# Revit family: Centro
name_source: partatom
category: Mechanical Equipment
units: mm (PartAtom-declared; Revit-internal decimal feet)

## family parameters
Always vertical = Yes
Classification = None
Cut with Voids When Loaded = No
Part Type = Normal
Room Calculation Point = No
Round Connector Dimension = Use Diameter
Shared = No
Work Plane-Based = No

## types (65) — shared parameters
00_20_Manufacturer = Blauberg
Description = For round channels
Frequency = 50 Hz
Load Classification = HVAC
Maintenance zone material = <By Category>
Manufacturer = Blauberg
Number of Fase = 1
URL = https://blaubergventilatoren.de
Voltage = 230 V
zero-valued in all types: Default Elevation

## per-type parameters (varying)
- Centro 315: Amperage=1 A; Apparent Load=202 VA; B=414 mm; B1=454 mm; B2=374 mm; Bracket=Yes; Bracket angle=No; Casing Material=Metal, painted, grey, matt RAL 7040; D=315 mm; D1=400 mm; D2=375 mm; Diameter=315 mm; Dy=311 mm; H=450 mm; H1=250 mm; Height=450 mm; L=276 mm; L1=40 mm  [stored 0.131234 ft]; L2=55 mm  [stored 0.180446 ft]; L3=40 mm  [stored 0.131234 ft]; L4=55 mm  [stored 0.180446 ft]; Length=276 mm; Maximum Air Flow=1340.0 m³/h; Power=200 W; R1=200 mm; R2=205 mm; Ry=158 mm; Sound pressure level at 3 m distance=48 dBA; Temperature of moving air=-25...+55 °C; Weight=4.85 kg; Width=454 mm; Сonnector=No; Сonnector E=Yes; Сonnector at an angle=No
- Centro 100: Amperage=0 A; Apparent Load=78 VA; B=270 mm; B1=310 mm; B2=230 mm; Bracket=Yes; Bracket angle=No; Casing Material=Metal, painted, grey, matt RAL 7040; D=100 mm  [stored 0.328084 ft]; D1=250 mm; D2=225 mm; Diameter=100 mm  [stored 0.328084 ft]; Dy=96 mm  [stored 0.314961 ft]; H=300 mm; H1=175 mm; Height=300 mm; L=230 mm; L1=30 mm  [stored 0.0984252 ft]; L2=27 mm  [stored 0.0885827 ft]; L3=30 mm  [stored 0.0984252 ft]; L4=45 mm  [stored 0.147638 ft]; Length=230 mm; Maximum Air Flow=250.0 m³/h; Power=80 W; R1=125 mm  [stored 0.410105 ft]; R2=130 mm  [stored 0.426509 ft]; Ry=50 mm  [stored 0.164042 ft]; Sound pressure level at 3 m distance=40 dBA; Temperature of moving air=-25...+55 °C; Weight=2.22 kg; Width=310 mm; Сonnector=No; Сonnector E=Yes; Сonnector at an angle=No
- Centro 100 L: Amperage=0 A; Apparent Load=87 VA; B=270 mm; B1=310 mm; B2=230 mm; Bracket=Yes; Bracket angle=No; Casing Material=Metal, painted, grey, matt RAL 7040; D=100 mm  [stored 0.328084 ft]; D1=250 mm; D2=225 mm; Diameter=100 mm  [stored 0.328084 ft]; Dy=96 mm  [stored 0.314961 ft]; H=300 mm; H1=175 mm; Height=300 mm; L=230 mm; L1=30 mm  [stored 0.0984252 ft]; L2=27 mm  [stored 0.0885827 ft]; L3=30 mm  [stored 0.0984252 ft]; L4=45 mm  [stored 0.147638 ft]; Length=230 mm; Maximum Air Flow=205.0 m³/h; Power=62 W; R1=125 mm  [stored 0.410105 ft]; R2=130 mm  [stored 0.426509 ft]; Ry=50 mm  [stored 0.164042 ft]; Sound pressure level at 3 m distance=36 dBA; Temperature of moving air=-25...+55 °C; Weight=2.22 kg; Width=310 mm; Сonnector=No; Сonnector E=Yes; Сonnector at an angle=No
- Centro 100 V2: Amperage=0 A; Apparent Load=58 VA; B=270 mm; B1=310 mm; B2=230 mm; Bracket=Yes; Bracket angle=No; Casing Material=Metal, painted, grey, matt RAL 7040; D=100 mm  [stored 0.328084 ft]; D1=250 mm; D2=225 mm; Diameter=100 mm  [stored 0.328084 ft]; Dy=96 mm  [stored 0.314961 ft]; H=300 mm; H1=175 mm; Height=300 mm; L=230 mm; L1=30 mm  [stored 0.0984252 ft]; L2=27 mm  [stored 0.0885827 ft]; L3=30 mm  [stored 0.0984252 ft]; L4=45 mm  [stored 0.147638 ft]; Length=230 mm; Maximum Air Flow=264.0 m³/h; Power=57 W; R1=125 mm  [stored 0.410105 ft]; R2=130 mm  [stored 0.426509 ft]; Ry=50 mm  [stored 0.164042 ft]; Sound pressure level at 3 m distance=38 dBA; Temperature of moving air=-25...+55 °C; Weight=2.22 kg; Width=310 mm; Сonnector=No; Сonnector E=Yes; Сonnector at an angle=No
- Centro 125: Amperage=0 A; Apparent Load=78 VA; B=270 mm; B1=310 mm; B2=230 mm; Bracket=Yes; Bracket angle=No; Casing Material=Metal, painted, grey, matt RAL 7040; D=125 mm  [stored 0.410105 ft]; D1=250 mm; D2=225 mm; Diameter=125 mm  [stored 0.410105 ft]; Dy=121 mm  [stored 0.396982 ft]; H=300 mm; H1=175 mm; Height=300 mm; L=220 mm; L1=30 mm  [stored 0.0984252 ft]; L2=27 mm  [stored 0.0885827 ft]; L3=30 mm  [stored 0.0984252 ft]; L4=45 mm  [stored 0.147638 ft]; Length=220 mm; Maximum Air Flow=264.0 m³/h; Power=79 W; R1=125 mm  [stored 0.410105 ft]; R2=130 mm  [stored 0.426509 ft]; Ry=63 mm; Sound pressure level at 3 m distance=40 dBA; Temperature of moving air=-25...+55 °C; Weight=2.20 kg; Width=310 mm; Сonnector=No; Сonnector E=Yes; Сonnector at an angle=No
- Centro 125 L: Amperage=0 A; Apparent Load=87 VA; B=270 mm; B1=310 mm; B2=230 mm; Bracket=Yes; Bracket angle=No; Casing Material=Metal, painted, grey, matt RAL 7040; D=125 mm  [stored 0.410105 ft]; D1=250 mm; D2=225 mm; Diameter=125 mm  [stored 0.410105 ft]; Dy=121 mm  [stored 0.396982 ft]; H=300 mm; H1=175 mm; Height=300 mm; L=220 mm; L1=30 mm  [stored 0.0984252 ft]; L2=27 mm  [stored 0.0885827 ft]; L3=30 mm  [stored 0.0984252 ft]; L4=45 mm  [stored 0.147638 ft]; Length=220 mm; Maximum Air Flow=260.0 m³/h; Power=61 W; R1=125 mm  [stored 0.410105 ft]; R2=130 mm  [stored 0.426509 ft]; Ry=63 mm; Sound pressure level at 3 m distance=36 dBA; Temperature of moving air=-25...+55 °C; Weight=2.20 kg; Width=310 mm; Сonnector=No; Сonnector E=Yes; Сonnector at an angle=No
- Centro 125 V2: Amperage=0 A; Apparent Load=60 VA; B=270 mm; B1=310 mm; B2=230 mm; Bracket=Yes; Bracket angle=No; Casing Material=Metal, painted, grey, matt RAL 7040; D=125 mm  [stored 0.410105 ft]; D1=250 mm; D2=225 mm; Diameter=125 mm  [stored 0.410105 ft]; Dy=121 mm  [stored 0.396982 ft]; H=300 mm; H1=175 mm; Height=300 mm; L=220 mm; L1=30 mm  [stored 0.0984252 ft]; L2=27 mm  [stored 0.0885827 ft]; L3=30 mm  [stored 0.0984252 ft]; L4=45 mm  [stored 0.147638 ft]; Length=220 mm; Maximum Air Flow=329.0 m³/h; Power=58 W; R1=125 mm  [stored 0.410105 ft]; R2=130 mm  [stored 0.426509 ft]; Ry=63 mm; Sound pressure level at 3 m distance=39 dBA; Temperature of moving air=-25...+55 °C; Weight=2.20 kg; Width=310 mm; Сonnector=No; Сonnector E=Yes; Сonnector at an angle=No
- Centro 150: Amperage=0 A; Apparent Load=81 VA; B=310 mm; B1=350 mm; B2=270 mm; Bracket=Yes; Bracket angle=No; Casing Material=Metal, painted, grey, matt RAL 7040; D=150 mm; D1=300 mm; D2=275 mm; Diameter=150 mm; Dy=146 mm; H=350 mm; H1=200 mm; Height=350 mm; L=286 mm; L1=30 mm  [stored 0.0984252 ft]; L2=30 mm  [stored 0.0984252 ft]; L3=30 mm  [stored 0.0984252 ft]; L4=45 mm  [stored 0.147638 ft]; Length=286 mm; Maximum Air Flow=460.0 m³/h; Power=80 W; R1=150 mm; R2=155 mm; Ry=75 mm  [stored 0.246063 ft]; Sound pressure level at 3 m distance=42 dBA; Temperature of moving air=-25...+55 °C; Weight=2.45 kg; Width=350 mm; Сonnector=No; Сonnector E=Yes; Сonnector at an angle=No
- Centro 150 V2: Amperage=0 A; Apparent Load=60 VA; B=310 mm; B1=350 mm; B2=270 mm; Bracket=Yes; Bracket angle=No; Casing Material=Metal, painted, grey, matt RAL 7040; D=150 mm; D1=300 mm; D2=275 mm; Diameter=150 mm; Dy=146 mm; H=350 mm; H1=200 mm; Height=350 mm; L=286 mm; L1=30 mm  [stored 0.0984252 ft]; L2=30 mm  [stored 0.0984252 ft]; L3=30 mm  [stored 0.0984252 ft]; L4=45 mm  [stored 0.147638 ft]; Length=286 mm; Maximum Air Flow=445.0 m³/h; Power=59 W; R1=150 mm; R2=155 mm; Ry=75 mm  [stored 0.246063 ft]; Sound pressure level at 3 m distance=40 dBA; Temperature of moving air=-25...+55 °C; Weight=2.45 kg; Width=350 mm; Сonnector=No; Сonnector E=Yes; Сonnector at an angle=No
- Centro 200: Amperage=0 A; Apparent Load=108 VA; B=354 mm; B1=394 mm; B2=314 mm; Bracket=Yes; Bracket angle=No; Casing Material=Metal, painted, grey, matt RAL 7040; D=200 mm; D1=340 mm; D2=315 mm; Diameter=200 mm; Dy=196 mm; H=390 mm; H1=220 mm; Height=390 mm; L=276 mm; L1=30 mm  [stored 0.0984252 ft]; L2=30 mm  [stored 0.0984252 ft]; L3=40 mm  [stored 0.131234 ft]; L4=55 mm  [stored 0.180446 ft]; Length=276 mm; Maximum Air Flow=780.0 m³/h; Power=107 W; R1=170 mm; R2=175 mm; Ry=100 mm  [stored 0.328084 ft]; Sound pressure level at 3 m distance=46 dBA; Temperature of moving air=-25...+55 °C; Weight=3.00 kg; Width=394 mm; Сonnector=No; Сonnector E=Yes; Сonnector at an angle=No
- Centro 200 max: Amperage=1 A; Apparent Load=175 VA; B=354 mm; B1=394 mm; B2=314 mm; Bracket=Yes; Bracket angle=No; Casing Material=Metal, painted, grey, matt RAL 7040; D=200 mm; D1=340 mm; D2=315 mm; Diameter=200 mm; Dy=196 mm; H=390 mm; H1=220 mm; Height=390 mm; L=276 mm; L1=30 mm  [stored 0.0984252 ft]; L2=30 mm  [stored 0.0984252 ft]; L3=40 mm  [stored 0.131234 ft]; L4=55 mm  [stored 0.180446 ft]; Length=276 mm; Maximum Air Flow=930.0 m³/h; Power=173 W; R1=170 mm; R2=175 mm; Ry=100 mm  [stored 0.328084 ft]; Sound pressure level at 3 m distance=48 dBA; Temperature of moving air=-25...+55 °C; Weight=3.00 kg; Width=394 mm; Сonnector=No; Сonnector E=Yes; Сonnector at an angle=No
- Centro 200 V2: Amperage=0 A; Apparent Load=99 VA; B=354 mm; B1=394 mm; B2=314 mm; Bracket=Yes; Bracket angle=No; Casing Material=Metal, painted, grey, matt RAL 7040; D=200 mm; D1=340 mm; D2=315 mm; Diameter=200 mm; Dy=196 mm; H=390 mm; H1=220 mm; Height=390 mm; L=276 mm; L1=30 mm  [stored 0.0984252 ft]; L2=30 mm  [stored 0.0984252 ft]; L3=40 mm  [stored 0.131234 ft]; L4=55 mm  [stored 0.180446 ft]; Length=276 mm; Maximum Air Flow=741.0 m³/h; Power=95 W; R1=170 mm; R2=175 mm; Ry=100 mm  [stored 0.328084 ft]; Sound pressure level at 3 m distance=42 dBA; Temperature of moving air=-25...+55 °C; Weight=3.00 kg; Width=394 mm; Сonnector=No; Сonnector E=Yes; Сonnector at an angle=No
- Centro 250 L: Amperage=0 A; Apparent Load=108 VA; B=354 mm; B1=394 mm; B2=314 mm; Bracket=Yes; Bracket angle=No; Casing Material=Metal, painted, grey, matt RAL 7040; D=250 mm; D1=340 mm; D2=315 mm; Diameter=250 mm; Dy=246 mm; H=390 mm; H1=220 mm; Height=390 mm; L=265 mm; L1=30 mm  [stored 0.0984252 ft]; L2=30 mm  [stored 0.0984252 ft]; L3=40 mm  [stored 0.131234 ft]; L4=55 mm  [stored 0.180446 ft]; Length=265 mm; Maximum Air Flow=865.0 m³/h; Power=108 W; R1=170 mm; R2=175 mm; Ry=125 mm  [stored 0.410105 ft]; Sound pressure level at 3 m distance=47 dBA; Temperature of moving air=-25...+55 °C; Weight=4.30 kg; Width=394 mm; Сonnector=No; Сonnector E=Yes; Сonnector at an angle=No
- Centro 250: Amperage=1 A; Apparent Load=175 VA; B=354 mm; B1=394 mm; B2=314 mm; Bracket=Yes; Bracket angle=No; Casing Material=Metal, painted, grey, matt RAL 7040; D=250 mm; D1=340 mm; D2=315 mm; Diameter=250 mm; Dy=246 mm; H=390 mm; H1=220 mm; Height=390 mm; L=265 mm; L1=30 mm  [stored 0.0984252 ft]; L2=30 mm  [stored 0.0984252 ft]; L3=40 mm  [stored 0.131234 ft]; L4=55 mm  [stored 0.180446 ft]; Length=265 mm; Maximum Air Flow=1080.0 m³/h; Power=173 W; R1=170 mm; R2=175 mm; Ry=125 mm  [stored 0.410105 ft]; Sound pressure level at 3 m distance=49 dBA; Temperature of moving air=-25...+55 °C; Weight=4.30 kg; Width=394 mm; Сonnector=No; Сonnector E=Yes; Сonnector at an angle=No
- Centro 250 V2: Amperage=1 A; Apparent Load=175 VA; B=354 mm; B1=394 mm; B2=314 mm; Bracket=Yes; Bracket angle=No; Casing Material=Metal, painted, grey, matt RAL 7040; D=250 mm; D1=340 mm; D2=315 mm; Diameter=250 mm; Dy=246 mm; H=390 mm; H1=220 mm; Height=390 mm; L=265 mm; L1=30 mm  [stored 0.0984252 ft]; L2=30 mm  [stored 0.0984252 ft]; L3=40 mm  [stored 0.131234 ft]; L4=55 mm  [stored 0.180446 ft]; Length=265 mm; Maximum Air Flow=1126.0 m³/h; Power=176 W; R1=170 mm; R2=175 mm; Ry=125 mm  [stored 0.410105 ft]; Sound pressure level at 3 m distance=46 dBA; Temperature of moving air=-25...+55 °C; Weight=4.30 kg; Width=394 mm; Сonnector=No; Сonnector E=Yes; Сonnector at an angle=No
- Centro 315 V2: Amperage=1 A; Apparent Load=175 VA; B=414 mm; B1=454 mm; B2=374 mm; Bracket=Yes; Bracket angle=No; Casing Material=Metal, painted, grey, matt RAL 7040; D=315 mm; D1=400 mm; D2=375 mm; Diameter=315 mm; Dy=311 mm; H=450 mm; H1=250 mm; Height=450 mm; L=276 mm; L1=40 mm  [stored 0.131234 ft]; L2=55 mm  [stored 0.180446 ft]; L3=40 mm  [stored 0.131234 ft]; L4=55 mm  [stored 0.180446 ft]; Length=276 mm; Maximum Air Flow=1268.0 m³/h; Power=173 W; R1=200 mm; R2=205 mm; Ry=158 mm; Sound pressure level at 3 m distance=48 dBA; Temperature of moving air=-25...+55 °C; Weight=4.85 kg; Width=454 mm; Сonnector=No; Сonnector E=Yes; Сonnector at an angle=No
- Centro 315 max: Amperage=1 A; Apparent Load=313 VA; B=414 mm; B1=454 mm; B2=374 mm; Bracket=Yes; Bracket angle=No; Casing Material=Metal, painted, grey, matt RAL 7040; D=315 mm; D1=400 mm; D2=375 mm; Diameter=315 mm; Dy=311 mm; H=450 mm; H1=250 mm; Height=450 mm; L=276 mm; L1=40 mm  [stored 0.131234 ft]; L2=55 mm  [stored 0.180446 ft]; L3=40 mm  [stored 0.131234 ft]; L4=55 mm  [stored 0.180446 ft]; Length=276 mm; Maximum Air Flow=1700.0 m³/h; Power=310 W; R1=200 mm; R2=205 mm; Ry=158 mm; Sound pressure level at 3 m distance=57 dBA; Temperature of moving air=-25...+45 °C; Weight=4.85 kg; Width=454 mm; Сonnector=No; Сonnector E=Yes; Сonnector at an angle=No
- Centro-MZ 100 L: Amperage=0 A; Apparent Load=44 VA; B=260 mm; B1=300 mm; B2=220 mm; Bracket=Yes; Bracket angle=No; Casing Material=Steel, galvanized; D=98 mm  [stored 0.321522 ft]; D1=245 mm; D2=220 mm; Diameter=98 mm  [stored 0.321522 ft]; Dy=94 mm  [stored 0.308399 ft]; H=295 mm; H1=173 mm; Height=325 mm; L=195 mm; L1=20 mm  [stored 0.0656168 ft]; L2=20 mm  [stored 0.0656168 ft]; L3=30 mm  [stored 0.0984252 ft]; L4=45 mm  [stored 0.147638 ft]; Length=195 mm; Maximum Air Flow=230.0 m³/h; Power=42 W; R1=123 mm  [stored 0.403543 ft]; R2=128 mm; Ry=49 mm  [stored 0.160761 ft]; Sound pressure level at 3 m distance=35 dBA; Temperature of moving air=-25...+55 °C; Weight=2.50 kg; Width=300 mm; Сonnector=Yes; Сonnector E=No; Сonnector at an angle=No
- Centro-MZ 125 L: Amperage=0 A; Apparent Load=85 VA; B=253 mm; B1=293 mm; B2=213 mm; Bracket=Yes; Bracket angle=No; Casing Material=Steel, galvanized; D=123 mm  [stored 0.403543 ft]; D1=237 mm; D2=212 mm; Diameter=123 mm  [stored 0.403543 ft]; Dy=119 mm  [stored 0.39042 ft]; H=287 mm; H1=169 mm; Height=317 mm; L=202 mm; L1=23 mm  [stored 0.0754593 ft]; L2=22 mm  [stored 0.0721785 ft]; L3=30 mm  [stored 0.0984252 ft]; L4=45 mm  [stored 0.147638 ft]; Length=202 mm; Maximum Air Flow=230.0 m³/h; Power=60 W; R1=119 mm  [stored 0.39042 ft]; R2=124 mm  [stored 0.406824 ft]; Ry=62 mm  [stored 0.203412 ft]; Sound pressure level at 3 m distance=35 dBA; Temperature of moving air=-25...+55 °C; Weight=3.16 kg; Width=293 mm; Сonnector=Yes; Сonnector E=No; Сonnector at an angle=No
- Centro-MZ 150: Amperage=0 A; Apparent Load=67 VA; B=290 mm; B1=330 mm; B2=250 mm; Bracket=Yes; Bracket angle=No; Casing Material=Steel, galvanized; D=149 mm; D1=274 mm; D2=249 mm; Diameter=149 mm; Dy=145 mm; H=324 mm; H1=187 mm; Height=354 mm; L=170 mm; L1=20 mm  [stored 0.0656168 ft]; L2=20 mm  [stored 0.0656168 ft]; L3=30 mm  [stored 0.0984252 ft]; L4=45 mm  [stored 0.147638 ft]; Length=170 mm; Maximum Air Flow=455.0 m³/h; Power=64 W; R1=137 mm  [stored 0.449475 ft]; R2=142 mm; Ry=75 mm  [stored 0.246063 ft]; Sound pressure level at 3 m distance=44 dBA; Temperature of moving air=-25...+50 °C; Weight=3.50 kg; Width=330 mm; Сonnector=Yes; Сonnector E=No; Сonnector at an angle=No
- Centro-MZ 150 max: Amperage=1 A; Apparent Load=129 VA; B=355 mm; B1=395 mm; B2=315 mm; Bracket=Yes; Bracket angle=No; Casing Material=Steel, galvanized; D=149 mm; D1=345 mm; D2=320 mm; Diameter=149 mm; Dy=145 mm; H=395 mm; H1=223 mm; Height=425 mm; L=230 mm; L1=20 mm  [stored 0.0656168 ft]; L2=20 mm  [stored 0.0656168 ft]; L3=40 mm  [stored 0.131234 ft]; L4=55 mm  [stored 0.180446 ft]; Length=230 mm; Maximum Air Flow=710.0 m³/h; Power=127 W; R1=173 mm; R2=178 mm; Ry=75 mm  [stored 0.246063 ft]; Sound pressure level at 3 m distance=48 dBA; Temperature of moving air=-25...+60 °C; Weight=5.60 kg; Width=395 mm; Сonnector=Yes; Сonnector E=No; Сonnector at an angle=No
- Centro-MZ 160: Amperage=0 A; Apparent Load=78 VA; B=294 mm; B1=334 mm; B2=254 mm; Bracket=Yes; Bracket angle=No; Casing Material=Steel, galvanized; D=158 mm; D1=278 mm; D2=253 mm; Diameter=158 mm; Dy=154 mm; H=328 mm; H1=189 mm; Height=358 mm; L=200 mm; L1=25 mm  [stored 0.082021 ft]; L2=23 mm  [stored 0.0754593 ft]; L3=30 mm  [stored 0.0984252 ft]; L4=45 mm  [stored 0.147638 ft]; Length=200 mm; Maximum Air Flow=455.0 m³/h; Power=78 W; R1=139 mm; R2=144 mm; Ry=79 mm; Sound pressure level at 3 m distance=46 dBA; Temperature of moving air=-25...+55 °C; Weight=3.44 kg; Width=334 mm; Сonnector=Yes; Сonnector E=No; Сonnector at an angle=No
- Centro-MZ 200 L: Amperage=1 A; Apparent Load=129 VA; B=340 mm; B1=380 mm; B2=300 mm; Bracket=Yes; Bracket angle=No; Casing Material=Steel, galvanized; D=198 mm; D1=332 mm; D2=307 mm; Diameter=198 mm; Dy=194 mm; H=382 mm; H1=216 mm; Height=412 mm; L=245 mm; L1=25 mm  [stored 0.082021 ft]; L2=29 mm  [stored 0.0951444 ft]; L3=40 mm  [stored 0.131234 ft]; L4=55 mm  [stored 0.180446 ft]; Length=245 mm; Maximum Air Flow=900.0 m³/h; Power=130 W; R1=166 mm; R2=171 mm; Ry=99 mm  [stored 0.324803 ft]; Sound pressure level at 3 m distance=48 dBA; Temperature of moving air=-25...+50 °C; Weight=5.43 kg; Width=380 mm; Сonnector=Yes; Сonnector E=No; Сonnector at an angle=No
- Centro-MZ 250 L: Amperage=1 A; Apparent Load=136 VA; B=340 mm; B1=380 mm; B2=300 mm; Bracket=Yes; Bracket angle=No; Casing Material=Steel, galvanized; D=249 mm; D1=332 mm; D2=307 mm; Diameter=249 mm; Dy=245 mm; H=382 mm; H1=216 mm; Height=412 mm; L=213 mm; L1=25 mm  [stored 0.082021 ft]; L2=29 mm  [stored 0.0951444 ft]; L3=40 mm  [stored 0.131234 ft]; L4=55 mm  [stored 0.180446 ft]; Length=213 mm; Maximum Air Flow=980.0 m³/h; Power=134 W; R1=166 mm; R2=171 mm; Ry=125 mm  [stored 0.410105 ft]; Sound pressure level at 3 m distance=51 dBA; Temperature of moving air=-25...+50 °C; Weight=5.25 kg; Width=380 mm; Сonnector=Yes; Сonnector E=No; Сonnector at an angle=No
- Centro-MZ 315 L: Amperage=1 A; Apparent Load=152 VA; B=410 mm; B1=450 mm; B2=370 mm; Bracket=Yes; Bracket angle=No; Casing Material=Steel, galvanized; D=313 mm; D1=402 mm; D2=377 mm; Diameter=313 mm; Dy=309 mm; H=452 mm; H1=251 mm; Height=482 mm; L=308 mm; L1=33 mm  [stored 0.108268 ft]; L2=55 mm  [stored 0.180446 ft]; L3=40 mm  [stored 0.131234 ft]; L4=55 mm  [stored 0.180446 ft]; Length=308 mm; Maximum Air Flow=1330.0 m³/h; Power=151 W; R1=201 mm; R2=206 mm; Ry=157 mm; Sound pressure level at 3 m distance=52 dBA; Temperature of moving air=-25...+50 °C; Weight=6.57 kg; Width=450 mm; Сonnector=Yes; Сonnector E=No; Сonnector at an angle=No
- Centro-MZ 100: Amperage=0 A; Apparent Load=64 VA; B=260 mm; B1=300 mm; B2=220 mm; Bracket=Yes; Bracket angle=No; Casing Material=Steel, galvanized; D=98 mm  [stored 0.321522 ft]; D1=245 mm; D2=220 mm; Diameter=98 mm  [stored 0.321522 ft]; Dy=94 mm  [stored 0.308399 ft]; H=295 mm; H1=173 mm; Height=325 mm; L=195 mm; L1=20 mm  [stored 0.0656168 ft]; L2=20 mm  [stored 0.0656168 ft]; L3=30 mm  [stored 0.0984252 ft]; L4=45 mm  [stored 0.147638 ft]; Length=195 mm; Maximum Air Flow=250.0 m³/h; Power=62 W; R1=123 mm  [stored 0.403543 ft]; R2=128 mm; Ry=49 mm  [stored 0.160761 ft]; Sound pressure level at 3 m distance=46 dBA; Temperature of moving air=-25...+55 °C; Weight=2.80 kg; Width=300 mm; Сonnector=Yes; Сonnector E=No; Сonnector at an angle=No
- Centro-MZ 125: Amperage=0 A; Apparent Load=78 VA; B=253 mm; B1=293 mm; B2=213 mm; Bracket=Yes; Bracket angle=No; Casing Material=Steel, galvanized; D=123 mm  [stored 0.403543 ft]; D1=237 mm; D2=212 mm; Diameter=123 mm  [stored 0.403543 ft]; Dy=119 mm  [stored 0.39042 ft]; H=287 mm; H1=169 mm; Height=317 mm; L=202 mm; L1=23 mm  [stored 0.0754593 ft]; L2=22 mm  [stored 0.0721785 ft]; L3=30 mm  [stored 0.0984252 ft]; L4=45 mm  [stored 0.147638 ft]; Length=202 mm; Maximum Air Flow=330.0 m³/h; Power=78 W; R1=119 mm  [stored 0.39042 ft]; R2=124 mm  [stored 0.406824 ft]; Ry=62 mm  [stored 0.203412 ft]; Sound pressure level at 3 m distance=46 dBA; Temperature of moving air=-25...+55 °C; Weight=3.16 kg; Width=293 mm; Сonnector=Yes; Сonnector E=No; Сonnector at an angle=No
- Centro-MZ 200: Amperage=1 A; Apparent Load=145 VA; B=340 mm; B1=380 mm; B2=300 mm; Bracket=Yes; Bracket angle=No; Casing Material=Steel, galvanized; D=198 mm; D1=332 mm; D2=307 mm; Diameter=198 mm; Dy=194 mm; H=382 mm; H1=216 mm; Height=412 mm; L=245 mm; L1=25 mm  [stored 0.082021 ft]; L2=29 mm  [stored 0.0951444 ft]; L3=40 mm  [stored 0.131234 ft]; L4=55 mm  [stored 0.180446 ft]; Length=245 mm; Maximum Air Flow=1000.0 m³/h; Power=144 W; R1=166 mm; R2=171 mm; Ry=99 mm  [stored 0.324803 ft]; Sound pressure level at 3 m distance=50 dBA; Temperature of moving air=-25...+50 °C; Weight=5.43 kg; Width=380 mm; Сonnector=Yes; Сonnector E=No; Сonnector at an angle=No
- Centro-MZ 250: Amperage=1 A; Apparent Load=152 VA; B=340 mm; B1=380 mm; B2=300 mm; Bracket=Yes; Bracket angle=No; Casing Material=Steel, galvanized; D=249 mm; D1=332 mm; D2=307 mm; Diameter=249 mm; Dy=245 mm; H=382 mm; H1=216 mm; Height=412 mm; L=213 mm; L1=25 mm  [stored 0.082021 ft]; L2=29 mm  [stored 0.0951444 ft]; L3=40 mm  [stored 0.131234 ft]; L4=55 mm  [stored 0.180446 ft]; Length=213 mm; Maximum Air Flow=1070.0 m³/h; Power=152 W; R1=166 mm; R2=171 mm; Ry=125 mm  [stored 0.410105 ft]; Sound pressure level at 3 m distance=52 dBA; Temperature of moving air=-25...+50 °C; Weight=5.25 kg; Width=380 mm; Сonnector=Yes; Сonnector E=No; Сonnector at an angle=No
- Centro-MZ 315: Amperage=1 A; Apparent Load=186 VA; B=410 mm; B1=450 mm; B2=370 mm; Bracket=Yes; Bracket angle=No; Casing Material=Steel, galvanized; D=313 mm; D1=402 mm; D2=377 mm; Diameter=313 mm; Dy=309 mm; H=452 mm; H1=251 mm; Height=482 mm; L=308 mm; L1=33 mm  [stored 0.108268 ft]; L2=55 mm  [stored 0.180446 ft]; L3=40 mm  [stored 0.131234 ft]; L4=55 mm  [stored 0.180446 ft]; Length=308 mm; Maximum Air Flow=1540.0 m³/h; Power=185 W; R1=201 mm; R2=206 mm; Ry=157 mm; Sound pressure level at 3 m distance=53 dBA; Temperature of moving air=-25...+45 °C; Weight=6.57 kg; Width=450 mm; Сonnector=Yes; Сonnector E=No; Сonnector at an angle=No
- Centro-M 100 L: Amperage=0 A; Apparent Load=55 VA; B=270 mm; B1=310 mm; B2=230 mm; Bracket=Yes; Bracket angle=No; Casing Material=Metal, painted, grey, matt RAL 7040; D=98 mm  [stored 0.321522 ft]; D1=225 mm; D2=200 mm; Diameter=98 mm  [stored 0.321522 ft]; Dy=94 mm  [stored 0.308399 ft]; H=275 mm; H1=163 mm; Height=305 mm; L=205 mm; L1=20 mm  [stored 0.0656168 ft]; L2=25 mm  [stored 0.082021 ft]; L3=30 mm  [stored 0.0984252 ft]; L4=45 mm  [stored 0.147638 ft]; Length=205 mm; Maximum Air Flow=233.0 m³/h; Power=45 W; R1=113 mm; R2=118 mm; Ry=49 mm  [stored 0.160761 ft]; Sound pressure level at 3 m distance=38 dBA; Temperature of moving air=-25...+45 °C; Weight=2.90 kg; Width=310 mm; Сonnector=Yes; Сonnector E=No; Сonnector at an angle=No
- Centro-M 100: Amperage=0 A; Apparent Load=64 VA; B=270 mm; B1=310 mm; B2=230 mm; Bracket=Yes; Bracket angle=No; Casing Material=Metal, painted, grey, matt RAL 7040; D=98 mm  [stored 0.321522 ft]; D1=225 mm; D2=200 mm; Diameter=98 mm  [stored 0.321522 ft]; Dy=94 mm  [stored 0.308399 ft]; H=275 mm; H1=163 mm; Height=305 mm; L=205 mm; L1=20 mm  [stored 0.0656168 ft]; L2=25 mm  [stored 0.082021 ft]; L3=30 mm  [stored 0.0984252 ft]; L4=45 mm  [stored 0.147638 ft]; Length=205 mm; Maximum Air Flow=279.0 m³/h; Power=60 W; R1=113 mm; R2=118 mm; Ry=49 mm  [stored 0.160761 ft]; Sound pressure level at 3 m distance=40 dBA; Temperature of moving air=-25...+45 °C; Weight=3.20 kg; Width=310 mm; Сonnector=Yes; Сonnector E=No; Сonnector at an angle=No
- Centro-M 125 L: Amperage=0 A; Apparent Load=58 VA; B=270 mm; B1=310 mm; B2=230 mm; Bracket=Yes; Bracket angle=No; Casing Material=Metal, painted, grey, matt RAL 7040; D=123 mm  [stored 0.403543 ft]; D1=225 mm; D2=200 mm; Diameter=123 mm  [stored 0.403543 ft]; Dy=119 mm  [stored 0.39042 ft]; H=275 mm; H1=163 mm; Height=305 mm; L=205 mm; L1=20 mm  [stored 0.0656168 ft]; L2=25 mm  [stored 0.082021 ft]; L3=30 mm  [stored 0.0984252 ft]; L4=45 mm  [stored 0.147638 ft]; Length=205 mm; Maximum Air Flow=326.0 m³/h; Power=47 W; R1=113 mm; R2=118 mm; Ry=62 mm  [stored 0.203412 ft]; Sound pressure level at 3 m distance=37 dBA; Temperature of moving air=-25...+45 °C; Weight=2.90 kg; Width=310 mm; Сonnector=Yes; Сonnector E=No; Сonnector at an angle=No
- Centro-M 125: Amperage=0 A; Apparent Load=67 VA; B=270 mm; B1=310 mm; B2=230 mm; Bracket=Yes; Bracket angle=No; Casing Material=Metal, painted, grey, matt RAL 7040; D=123 mm  [stored 0.403543 ft]; D1=225 mm; D2=200 mm; Diameter=123 mm  [stored 0.403543 ft]; Dy=119 mm  [stored 0.39042 ft]; H=275 mm; H1=163 mm; Height=305 mm; L=205 mm; L1=20 mm  [stored 0.0656168 ft]; L2=25 mm  [stored 0.082021 ft]; L3=30 mm  [stored 0.0984252 ft]; L4=45 mm  [stored 0.147638 ft]; Length=205 mm; Maximum Air Flow=360.0 m³/h; Power=64 W; R1=113 mm; R2=118 mm; Ry=62 mm  [stored 0.203412 ft]; Sound pressure level at 3 m distance=40 dBA; Temperature of moving air=-25...+45 °C; Weight=3.20 kg; Width=310 mm; Сonnector=Yes; Сonnector E=No; Сonnector at an angle=No
- Centro-M 150: Amperage=0 A; Apparent Load=104 VA; B=355 mm; B1=395 mm; B2=315 mm; Bracket=Yes; Bracket angle=No; Casing Material=Metal, painted, grey, matt RAL 7040; D=149 mm; D1=345 mm; D2=320 mm; Diameter=149 mm; Dy=145 mm; H=395 mm; H1=223 mm; Height=425 mm; L=200 mm; L1=20 mm  [stored 0.0656168 ft]; L2=20 mm  [stored 0.0656168 ft]; L3=40 mm  [stored 0.131234 ft]; L4=55 mm  [stored 0.180446 ft]; Length=200 mm; Maximum Air Flow=580.0 m³/h; Power=100 W; R1=173 mm; R2=178 mm; Ry=75 mm  [stored 0.246063 ft]; Sound pressure level at 3 m distance=45 dBA; Temperature of moving air=-25...+45 °C; Weight=5.10 kg; Width=395 mm; Сonnector=Yes; Сonnector E=No; Сonnector at an angle=No
- Centro-M 150 max: Amperage=1 A; Apparent Load=127 VA; B=355 mm; B1=395 mm; B2=315 mm; Bracket=Yes; Bracket angle=No; Casing Material=Metal, painted, grey, matt RAL 7040; D=149 mm; D1=345 mm; D2=320 mm; Diameter=149 mm; Dy=145 mm; H=395 mm; H1=223 mm; Height=425 mm; L=230 mm; L1=20 mm  [stored 0.0656168 ft]; L2=20 mm  [stored 0.0656168 ft]; L3=40 mm  [stored 0.131234 ft]; L4=55 mm  [stored 0.180446 ft]; Length=230 mm; Maximum Air Flow=710.0 m³/h; Power=127 W; R1=173 mm; R2=178 mm; Ry=75 mm  [stored 0.246063 ft]; Sound pressure level at 3 m distance=48 dBA; Temperature of moving air=-25...+45 °C; Weight=5.60 kg; Width=395 mm; Сonnector=Yes; Сonnector E=No; Сonnector at an angle=No
- Centro-M 160: Amperage=0 A; Apparent Load=101 VA; B=320 mm; B1=360 mm; B2=280 mm; Bracket=Yes; Bracket angle=No; Casing Material=Metal, painted, grey, matt RAL 7040; D=159 mm; D1=305 mm; D2=280 mm; Diameter=159 mm; Dy=155 mm; H=355 mm; H1=203 mm; Height=385 mm; L=220 mm; L1=25 mm  [stored 0.082021 ft]; L2=25 mm  [stored 0.082021 ft]; L3=30 mm  [stored 0.0984252 ft]; L4=45 mm  [stored 0.147638 ft]; Length=220 mm; Maximum Air Flow=567.0 m³/h; Power=99 W; R1=153 mm; R2=158 mm; Ry=80 mm  [stored 0.262467 ft]; Sound pressure level at 3 m distance=45 dBA; Temperature of moving air=-25...+45 °C; Weight=5.00 kg; Width=360 mm; Сonnector=Yes; Сonnector E=No; Сonnector at an angle=No
- Centro-M 160 max: Amperage=1 A; Apparent Load=122 VA; B=350 mm; B1=390 mm; B2=310 mm; Bracket=Yes; Bracket angle=No; Casing Material=Metal, painted, grey, matt RAL 7040; D=158 mm; D1=340 mm; D2=315 mm; Diameter=158 mm; Dy=154 mm; H=390 mm; H1=220 mm; Height=420 mm; L=245 mm; L1=25 mm  [stored 0.082021 ft]; L2=20 mm  [stored 0.0656168 ft]; L3=40 mm  [stored 0.131234 ft]; L4=55 mm  [stored 0.180446 ft]; Length=245 mm; Maximum Air Flow=690.0 m³/h; Power=121 W; R1=170 mm; R2=175 mm; Ry=79 mm; Sound pressure level at 3 m distance=48 dBA; Temperature of moving air=-25...+45 °C; Weight=6.40 kg; Width=390 mm; Сonnector=Yes; Сonnector E=No; Сonnector at an angle=No
- Centro-M 200: Amperage=1 A; Apparent Load=136 VA; B=355 mm; B1=395 mm; B2=315 mm; Bracket=Yes; Bracket angle=No; Casing Material=Metal, painted, grey, matt RAL 7040; D=198 mm; D1=345 mm; D2=320 mm; Diameter=198 mm; Dy=194 mm; H=395 mm; H1=223 mm; Height=425 mm; L=255 mm; L1=25 mm  [stored 0.082021 ft]; L2=30 mm  [stored 0.0984252 ft]; L3=40 mm  [stored 0.131234 ft]; L4=55 mm  [stored 0.180446 ft]; Length=255 mm; Maximum Air Flow=1070.0 m³/h; Power=135 W; R1=173 mm; R2=178 mm; Ry=99 mm  [stored 0.324803 ft]; Sound pressure level at 3 m distance=48 dBA; Temperature of moving air=-25...+45 °C; Weight=6.60 kg; Width=395 mm; Сonnector=Yes; Сonnector E=No; Сonnector at an angle=No
- Centro-M 200 max: Amperage=1 A; Apparent Load=193 VA; B=355 mm; B1=395 mm; B2=315 mm; Bracket=Yes; Bracket angle=No; Casing Material=Metal, painted, grey, matt RAL 7040; D=198 mm; D1=345 mm; D2=320 mm; Diameter=198 mm; Dy=194 mm; H=395 mm; H1=223 mm; Height=425 mm; L=255 mm; L1=25 mm  [stored 0.082021 ft]; L2=30 mm  [stored 0.0984252 ft]; L3=40 mm  [stored 0.131234 ft]; L4=55 mm  [stored 0.180446 ft]; Length=255 mm; Maximum Air Flow=1150.0 m³/h; Power=193 W; R1=173 mm; R2=178 mm; Ry=99 mm  [stored 0.324803 ft]; Sound pressure level at 3 m distance=49 dBA; Temperature of moving air=-25...+45 °C; Weight=8.30 kg; Width=395 mm; Сonnector=Yes; Сonnector E=No; Сonnector at an angle=No
- Centro-M 250 E: Amperage=0 A; Apparent Load=108 VA; B=355 mm; B1=395 mm; B2=315 mm; Bracket=Yes; Bracket angle=No; Casing Material=Metal, painted, grey, matt RAL 7040; D=248 mm; D1=345 mm; D2=320 mm; Diameter=248 mm; Dy=244 mm; H=395 mm; H1=223 mm; Height=425 mm; L=250 mm; L1=25 mm  [stored 0.082021 ft]; L2=30 mm  [stored 0.0984252 ft]; L3=40 mm  [stored 0.131234 ft]; L4=55 mm  [stored 0.180446 ft]; Length=250 mm; Maximum Air Flow=900.0 m³/h; Power=95 W; R1=173 mm; R2=178 mm; Ry=124 mm  [stored 0.406824 ft]; Sound pressure level at 3 m distance=47 dBA; Temperature of moving air=-25...+45 °C; Weight=6.20 kg; Width=395 mm; Сonnector=Yes; Сonnector E=No; Сonnector at an angle=No
- Centro-M 250: Amperage=1 A; Apparent Load=196 VA; B=355 mm; B1=395 mm; B2=315 mm; Bracket=Yes; Bracket angle=No; Casing Material=Metal, painted, grey, matt RAL 7040; D=248 mm; D1=345 mm; D2=320 mm; Diameter=248 mm; Dy=244 mm; H=395 mm; H1=223 mm; Height=425 mm; L=250 mm; L1=25 mm  [stored 0.082021 ft]; L2=30 mm  [stored 0.0984252 ft]; L3=40 mm  [stored 0.131234 ft]; L4=55 mm  [stored 0.180446 ft]; Length=250 mm; Maximum Air Flow=1420.0 m³/h; Power=194 W; R1=173 mm; R2=178 mm; Ry=124 mm  [stored 0.406824 ft]; Sound pressure level at 3 m distance=50 dBA; Temperature of moving air=-25...+45 °C; Weight=8.40 kg; Width=395 mm; Сonnector=Yes; Сonnector E=No; Сonnector at an angle=No
- Centro-M 315: Amperage=1 A; Apparent Load=177 VA; B=415 mm; B1=455 mm; B2=375 mm; Bracket=Yes; Bracket angle=No; Casing Material=Metal, painted, grey, matt RAL 7040; D=314 mm; D1=405 mm; D2=380 mm; Diameter=314 mm; Dy=310 mm; H=455 mm; H1=253 mm; Height=485 mm; L=260 mm; L1=30 mm  [stored 0.0984252 ft]; L2=30 mm  [stored 0.0984252 ft]; L3=40 mm  [stored 0.131234 ft]; L4=55 mm  [stored 0.180446 ft]; Length=260 mm; Maximum Air Flow=1440.0 m³/h; Power=171 W; R1=203 mm; R2=208 mm; Ry=157 mm; Sound pressure level at 3 m distance=52 dBA; Temperature of moving air=-25...+45 °C; Weight=8.00 kg; Width=455 mm; Сonnector=Yes; Сonnector E=No; Сonnector at an angle=No
- Centro-M 315 max: Amperage=1 A; Apparent Load=308 VA; B=415 mm; B1=455 mm; B2=375 mm; Bracket=Yes; Bracket angle=No; Casing Material=Metal, painted, grey, matt RAL 7040; D=314 mm; D1=405 mm; D2=380 mm; Diameter=314 mm; Dy=310 mm; H=455 mm; H1=253 mm; Height=485 mm; L=290 mm; L1=30 mm  [stored 0.0984252 ft]; L2=30 mm  [stored 0.0984252 ft]; L3=40 mm  [stored 0.131234 ft]; L4=55 mm  [stored 0.180446 ft]; Length=290 mm; Maximum Air Flow=1920.0 m³/h; Power=295 W; R1=203 mm; R2=208 mm; Ry=157 mm; Sound pressure level at 3 m distance=54 dBA; Temperature of moving air=-25...+45 °C; Weight=8.80 kg; Width=455 mm; Сonnector=Yes; Сonnector E=No; Сonnector at an angle=No
- Centro-M 355 L: Amperage=1 A; Apparent Load=244 VA; B=522 mm; B1=552 mm; B2=472 mm; Bracket=No; Bracket angle=Yes; Casing Material=Metal, painted, grey, matt RAL 7040; D=353 mm; D1=460 mm; D2=435 mm; Diameter=353 mm; Dy=349 mm; H=510 mm; H1=280 mm; Height=510 mm; L=506 mm; L1=60 mm  [stored 0.19685 ft]; L2=60 mm  [stored 0.19685 ft]; L3=70 mm  [stored 0.229659 ft]; L4=85 mm  [stored 0.278871 ft]; Length=506 mm; Maximum Air Flow=2250.0 m³/h; Power=233 W; R1=230 mm; R2=235 mm; Ry=177 mm; Sound pressure level at 3 m distance=58 dBA; Temperature of moving air=-25...+45 °C; Weight=18.80 kg; Width=552 mm; Сonnector=No; Сonnector E=No; Сonnector at an angle=Yes
- Centro-M 400: Amperage=2 A; Apparent Load=513 VA; B=634 mm; B1=664 mm; B2=584 mm; Bracket=No; Bracket angle=Yes; Casing Material=Metal, painted, grey, matt RAL 7040; D=398 mm; D1=570 mm; D2=545 mm; Diameter=398 mm; Dy=394 mm; H=620 mm; H1=335 mm; Height=620 mm; L=570 mm; L1=60 mm  [stored 0.19685 ft]; L2=60 mm  [stored 0.19685 ft]; L3=70 mm  [stored 0.229659 ft]; L4=85 mm  [stored 0.278871 ft]; Length=570 mm; Maximum Air Flow=3090.0 m³/h; Power=460 W; R1=285 mm; R2=290 mm; Ry=199 mm; Sound pressure level at 3 m distance=61 dBA; Temperature of moving air=-40...+80°C; Weight=25.10 kg; Width=664 mm; Сonnector=No; Сonnector E=No; Сonnector at an angle=Yes
- Centro-M 450: Amperage=3 A; Apparent Load=665 VA; B=670 mm; B1=700 mm; B2=620 mm; Bracket=No; Bracket angle=Yes; Casing Material=Metal, painted, grey, matt RAL 7040; D=448 mm; D1=608 mm; D2=583 mm; Diameter=448 mm; Dy=444 mm; H=658 mm; H1=354 mm; Height=658 mm; L=644 mm; L1=60 mm  [stored 0.19685 ft]; L2=60 mm  [stored 0.19685 ft]; L3=80 mm  [stored 0.262467 ft]; L4=95 mm  [stored 0.31168 ft]; Length=644 mm; Maximum Air Flow=5300.0 m³/h; Power=665 W; R1=304 mm; R2=309 mm; Ry=224 mm; Sound pressure level at 3 m distance=65 dBA; Temperature of moving air=-40...+70 °C; Weight=27.26 kg; Width=700 mm; Сonnector=No; Сonnector E=No; Сonnector at an angle=Yes
- Centro EC 100: Amperage=1 A; Apparent Load=143 VA; B=270 mm; B1=310 mm; B2=230 mm; Bracket=Yes; Bracket angle=No; Casing Material=Пластмасса, непрозрачная, серая; D=100 mm  [stored 0.328084 ft]; D1=250 mm; D2=225 mm; Diameter=100 mm  [stored 0.328084 ft]; Dy=96 mm  [stored 0.314961 ft]; H=300 mm; H1=175 mm; Height=300 mm; L=230 mm; L1=30 mm  [stored 0.0984252 ft]; L2=27 mm  [stored 0.0885827 ft]; L3=30 mm  [stored 0.0984252 ft]; L4=45 mm  [stored 0.147638 ft]; Length=230 mm; Maximum Air Flow=340.0 m³/h; Power=82 W; R1=125 mm  [stored 0.410105 ft]; R2=130 mm  [stored 0.426509 ft]; Ry=50 mm  [stored 0.164042 ft]; Sound pressure level at 3 m distance=40 dBA; Temperature of moving air=-25...+60 °C; Weight=2.00 kg; Width=310 mm; Сonnector=No; Сonnector E=Yes; Сonnector at an angle=No
- Centro EC 125: Amperage=1 A; Apparent Load=147 VA; B=270 mm; B1=310 mm; B2=230 mm; Bracket=Yes; Bracket angle=No; Casing Material=Пластмасса, непрозрачная, серая; D=125 mm  [stored 0.410105 ft]; D1=250 mm; D2=225 mm; Diameter=125 mm  [stored 0.410105 ft]; Dy=121 mm  [stored 0.396982 ft]; H=300 mm; H1=175 mm; Height=300 mm; L=220 mm; L1=30 mm  [stored 0.0984252 ft]; L2=27 mm  [stored 0.0885827 ft]; L3=30 mm  [stored 0.0984252 ft]; L4=45 mm  [stored 0.147638 ft]; Length=220 mm; Maximum Air Flow=420.0 m³/h; Power=84 W; R1=125 mm  [stored 0.410105 ft]; R2=130 mm  [stored 0.426509 ft]; Ry=63 mm; Sound pressure level at 3 m distance=42 dBA; Temperature of moving air=-25...+60 °C; Weight=2.20 kg; Width=310 mm; Сonnector=No; Сonnector E=Yes; Сonnector at an angle=No
- Centro EC 150: Amperage=1 A; Apparent Load=145 VA; B=310 mm; B1=350 mm; B2=270 mm; Bracket=Yes; Bracket angle=No; Casing Material=Пластмасса, непрозрачная, серая; D=150 mm; D1=300 mm; D2=275 mm; Diameter=150 mm; Dy=146 mm; H=350 mm; H1=200 mm; Height=350 mm; L=286 mm; L1=30 mm  [stored 0.0984252 ft]; L2=30 mm  [stored 0.0984252 ft]; L3=30 mm  [stored 0.0984252 ft]; L4=45 mm  [stored 0.147638 ft]; Length=286 mm; Maximum Air Flow=630.0 m³/h; Power=82 W; R1=150 mm; R2=155 mm; Ry=75 mm  [stored 0.246063 ft]; Sound pressure level at 3 m distance=45 dBA; Temperature of moving air=-25...+60 °C; Weight=2.50 kg; Width=350 mm; Сonnector=No; Сonnector E=Yes; Сonnector at an angle=No
- Centro EC 200: Amperage=1 A; Apparent Load=147 VA; B=354 mm; B1=394 mm; B2=314 mm; Bracket=Yes; Bracket angle=No; Casing Material=Пластмасса, непрозрачная, серая; D=200 mm; D1=340 mm; D2=315 mm; Diameter=200 mm; Dy=196 mm; H=390 mm; H1=220 mm; Height=390 mm; L=276 mm; L1=30 mm  [stored 0.0984252 ft]; L2=30 mm  [stored 0.0984252 ft]; L3=40 mm  [stored 0.131234 ft]; L4=55 mm  [stored 0.180446 ft]; Length=276 mm; Maximum Air Flow=885.0 m³/h; Power=84 W; R1=170 mm; R2=175 mm; Ry=100 mm  [stored 0.328084 ft]; Sound pressure level at 3 m distance=47 dBA; Temperature of moving air=-25...+60 °C; Weight=3.00 kg; Width=394 mm; Сonnector=No; Сonnector E=Yes; Сonnector at an angle=No
- Centro EC 250: Amperage=1 A; Apparent Load=253 VA; B=354 mm; B1=394 mm; B2=314 mm; Bracket=Yes; Bracket angle=No; Casing Material=Пластмасса, непрозрачная, серая; D=250 mm; D1=340 mm; D2=315 mm; Diameter=250 mm; Dy=246 mm; H=390 mm; H1=220 mm; Height=390 mm; L=265 mm; L1=30 mm  [stored 0.0984252 ft]; L2=30 mm  [stored 0.0984252 ft]; L3=40 mm  [stored 0.131234 ft]; L4=55 mm  [stored 0.180446 ft]; Length=265 mm; Maximum Air Flow=1250.0 m³/h; Power=165 W; R1=170 mm; R2=175 mm; Ry=125 mm  [stored 0.410105 ft]; Sound pressure level at 3 m distance=48 dBA; Temperature of moving air=-25...+60 °C; Weight=4.30 kg; Width=394 mm; Сonnector=No; Сonnector E=Yes; Сonnector at an angle=No
- Centro EC 315: Amperage=1 A; Apparent Load=265 VA; B=414 mm; B1=454 mm; B2=374 mm; Bracket=Yes; Bracket angle=No; Casing Material=Пластмасса, непрозрачная, серая; D=315 mm; D1=400 mm; D2=375 mm; Diameter=315 mm; Dy=311 mm; H=450 mm; H1=250 mm; Height=450 mm; L=276 mm; L1=40 mm  [stored 0.131234 ft]; L2=55 mm  [stored 0.180446 ft]; L3=40 mm  [stored 0.131234 ft]; L4=55 mm  [stored 0.180446 ft]; Length=276 mm; Maximum Air Flow=1500.0 m³/h; Power=165 W; R1=200 mm; R2=205 mm; Ry=158 mm; Sound pressure level at 3 m distance=48 dBA; Temperature of moving air=-25...+60 °C; Weight=4.90 kg; Width=454 mm; Сonnector=No; Сonnector E=Yes; Сonnector at an angle=No
- Centro-M EC 100: Amperage=1 A; Apparent Load=161 VA; B=270 mm; B1=310 mm; B2=230 mm; Bracket=Yes; Bracket angle=No; Casing Material=Metal, painted, grey, matt RAL 7040; D=98 mm  [stored 0.321522 ft]; D1=255 mm; D2=230 mm; Diameter=98 mm  [stored 0.321522 ft]; Dy=94 mm  [stored 0.308399 ft]; H=305 mm; H1=178 mm; Height=335 mm; L=203 mm; L1=20 mm  [stored 0.0656168 ft]; L2=25 mm  [stored 0.082021 ft]; L3=30 mm  [stored 0.0984252 ft]; L4=45 mm  [stored 0.147638 ft]; Length=203 mm; Maximum Air Flow=345.0 m³/h; Power=90 W; R1=128 mm; R2=133 mm; Ry=49 mm  [stored 0.160761 ft]; Sound pressure level at 3 m distance=44 dBA; Temperature of moving air=-25...+60 °C; Weight=3.45 kg; Width=310 mm; Сonnector=Yes; Сonnector E=No; Сonnector at an angle=No
- Centro-M EC 125: Amperage=1 A; Apparent Load=133 VA; B=270 mm; B1=310 mm; B2=230 mm; Bracket=Yes; Bracket angle=No; Casing Material=Metal, painted, grey, matt RAL 7040; D=123 mm  [stored 0.403543 ft]; D1=255 mm; D2=230 mm; Diameter=123 mm  [stored 0.403543 ft]; Dy=119 mm  [stored 0.39042 ft]; H=305 mm; H1=178 mm; Height=335 mm; L=203 mm; L1=20 mm  [stored 0.0656168 ft]; L2=25 mm  [stored 0.082021 ft]; L3=30 mm  [stored 0.0984252 ft]; L4=45 mm  [stored 0.147638 ft]; Length=203 mm; Maximum Air Flow=480.0 m³/h; Power=83 W; R1=128 mm; R2=133 mm; Ry=62 mm  [stored 0.203412 ft]; Sound pressure level at 3 m distance=45 dBA; Temperature of moving air=-25...+60 °C; Weight=3.58 kg; Width=310 mm; Сonnector=Yes; Сonnector E=No; Сonnector at an angle=No
- Centro-M EC 150: Amperage=1 A; Apparent Load=205 VA; B=320 mm; B1=360 mm; B2=280 mm; Bracket=Yes; Bracket angle=No; Casing Material=Metal, painted, grey, matt RAL 7040; D=149 mm; D1=305 mm; D2=280 mm; Diameter=149 mm; Dy=145 mm; H=355 mm; H1=203 mm; Height=385 mm; L=240 mm; L1=25 mm  [stored 0.082021 ft]; L2=25 mm  [stored 0.082021 ft]; L3=30 mm  [stored 0.0984252 ft]; L4=45 mm  [stored 0.147638 ft]; Length=240 mm; Maximum Air Flow=700.0 m³/h; Power=107 W; R1=153 mm; R2=158 mm; Ry=75 mm  [stored 0.246063 ft]; Sound pressure level at 3 m distance=48 dBA; Temperature of moving air=-25...+60 °C; Weight=4.70 kg; Width=360 mm; Сonnector=Yes; Сonnector E=No; Сonnector at an angle=No
- Centro-M EC 160: Amperage=1 A; Apparent Load=207 VA; B=320 mm; B1=360 mm; B2=280 mm; Bracket=Yes; Bracket angle=No; Casing Material=Metal, painted, grey, matt RAL 7040; D=159 mm; D1=305 mm; D2=280 mm; Diameter=159 mm; Dy=155 mm; H=355 mm; H1=203 mm; Height=385 mm; L=240 mm; L1=25 mm  [stored 0.082021 ft]; L2=25 mm  [stored 0.082021 ft]; L3=30 mm  [stored 0.0984252 ft]; L4=45 mm  [stored 0.147638 ft]; Length=240 mm; Maximum Air Flow=785.0 m³/h; Power=108 W; R1=153 mm; R2=158 mm; Ry=80 mm  [stored 0.262467 ft]; Sound pressure level at 3 m distance=48 dBA; Temperature of moving air=-25...+60 °C; Weight=4.90 kg; Width=360 mm; Сonnector=Yes; Сonnector E=No; Сonnector at an angle=No
- Centro-M EC 200: Amperage=1 A; Apparent Load=145 VA; B=355 mm; B1=395 mm; B2=315 mm; Bracket=Yes; Bracket angle=No; Casing Material=Metal, painted, grey, matt RAL 7040; D=198 mm; D1=345 mm; D2=320 mm; Diameter=198 mm; Dy=194 mm; H=395 mm; H1=223 mm; Height=425 mm; L=245 mm; L1=25 mm  [stored 0.082021 ft]; L2=30 mm  [stored 0.0984252 ft]; L3=40 mm  [stored 0.131234 ft]; L4=55 mm  [stored 0.180446 ft]; Length=245 mm; Maximum Air Flow=845.0 m³/h; Power=83 W; R1=173 mm; R2=178 mm; Ry=99 mm  [stored 0.324803 ft]; Sound pressure level at 3 m distance=47 dBA; Temperature of moving air=-25...+60 °C; Weight=5.70 kg; Width=395 mm; Сonnector=Yes; Сonnector E=No; Сonnector at an angle=No
- Centro-M EC 200 max: Amperage=1 A; Apparent Load=170 VA; B=355 mm; B1=395 mm; B2=315 mm; Bracket=Yes; Bracket angle=No; Casing Material=Metal, painted, grey, matt RAL 7040; D=198 mm; D1=345 mm; D2=320 mm; Diameter=198 mm; Dy=194 mm; H=395 mm; H1=223 mm; Height=425 mm; L=255 mm; L1=25 mm  [stored 0.082021 ft]; L2=30 mm  [stored 0.0984252 ft]; L3=40 mm  [stored 0.131234 ft]; L4=55 mm  [stored 0.180446 ft]; Length=255 mm; Maximum Air Flow=1010.0 m³/h; Power=100 W; R1=173 mm; R2=178 mm; Ry=99 mm  [stored 0.324803 ft]; Sound pressure level at 3 m distance=48 dBA; Temperature of moving air=-25...+60 °C; Weight=5.70 kg; Width=395 mm; Сonnector=Yes; Сonnector E=No; Сonnector at an angle=No
- Centro-M EC 250: Amperage=1 A; Apparent Load=265 VA; B=355 mm; B1=395 mm; B2=315 mm; Bracket=Yes; Bracket angle=No; Casing Material=Metal, painted, grey, matt RAL 7040; D=248 mm; D1=345 mm; D2=320 mm; Diameter=248 mm; Dy=244 mm; H=395 mm; H1=223 mm; Height=425 mm; L=250 mm; L1=25 mm  [stored 0.082021 ft]; L2=30 mm  [stored 0.0984252 ft]; L3=40 mm  [stored 0.131234 ft]; L4=55 mm  [stored 0.180446 ft]; Length=250 mm; Maximum Air Flow=1230.0 m³/h; Power=164 W; R1=173 mm; R2=178 mm; Ry=124 mm  [stored 0.406824 ft]; Sound pressure level at 3 m distance=46 dBA; Temperature of moving air=-25...+60 °C; Weight=5.09 kg; Width=395 mm; Сonnector=Yes; Сonnector E=No; Сonnector at an angle=No
- Centro-M EC 315: Amperage=1 A; Apparent Load=265 VA; B=415 mm; B1=455 mm; B2=375 mm; Bracket=Yes; Bracket angle=No; Casing Material=Metal, painted, grey, matt RAL 7040; D=314 mm; D1=405 mm; D2=380 mm; Diameter=314 mm; Dy=310 mm; H=455 mm; H1=253 mm; Height=485 mm; L=260 mm; L1=30 mm  [stored 0.0984252 ft]; L2=30 mm  [stored 0.0984252 ft]; L3=40 mm  [stored 0.131234 ft]; L4=55 mm  [stored 0.180446 ft]; Length=260 mm; Maximum Air Flow=1370.0 m³/h; Power=164 W; R1=203 mm; R2=208 mm; Ry=157 mm; Sound pressure level at 3 m distance=48 dBA; Temperature of moving air=-25...+60 °C; Weight=7.30 kg; Width=455 mm; Сonnector=Yes; Сonnector E=No; Сonnector at an angle=No
- Centro-M EC 315 max: Amperage=1 A; Apparent Load=331 VA; B=472 mm; B1=512 mm; B2=432 mm; Bracket=No; Bracket angle=Yes; Casing Material=Metal, painted, grey, matt RAL 7040; D=314 mm; D1=410 mm; D2=385 mm; Diameter=314 mm; Dy=310 mm; H=460 mm; H1=255 mm; Height=460 mm; L=462 mm; L1=60 mm  [stored 0.19685 ft]; L2=60 mm  [stored 0.19685 ft]; L3=50 mm  [stored 0.164042 ft]; L4=65 mm  [stored 0.213255 ft]; Length=462 mm; Maximum Air Flow=1820.0 m³/h; Power=183 W; R1=205 mm; R2=210 mm; Ry=157 mm; Sound pressure level at 3 m distance=49 dBA; Temperature of moving air=-25...+60 °C; Weight=9.42 kg; Width=512 mm; Сonnector=No; Сonnector E=No; Сonnector at an angle=Yes
- Centro-M EC 355: Amperage=3 A; Apparent Load=706 VA; B=522 mm; B1=552 mm; B2=472 mm; Bracket=No; Bracket angle=Yes; Casing Material=Metal, painted, grey, matt RAL 7040; D=353 mm; D1=460 mm; D2=435 mm; Diameter=353 mm; Dy=349 mm; H=510 mm; H1=280 mm; Height=510 mm; L=562 mm; L1=60 mm  [stored 0.19685 ft]; L2=60 mm  [stored 0.19685 ft]; L3=70 mm  [stored 0.229659 ft]; L4=85 mm  [stored 0.278871 ft]; Length=562 mm; Maximum Air Flow=3450.0 m³/h; Power=693 W; R1=230 mm; R2=235 mm; Ry=177 mm; Sound pressure level at 3 m distance=62 dBA; Temperature of moving air=-25...+60 °C; Weight=15.80 kg; Width=552 mm; Сonnector=No; Сonnector E=No; Сonnector at an angle=Yes
- Centro-M EC 400: Amperage=3 A; Apparent Load=720 VA; B=634 mm; B1=664 mm; B2=584 mm; Bracket=No; Bracket angle=Yes; Casing Material=Metal, painted, grey, matt RAL 7040; D=398 mm; D1=570 mm; D2=545 mm; Diameter=398 mm; Dy=394 mm; H=620 mm; H1=335 mm; Height=620 mm; L=599 mm; L1=60 mm  [stored 0.19685 ft]; L2=60 mm  [stored 0.19685 ft]; L3=70 mm  [stored 0.229659 ft]; L4=85 mm  [stored 0.278871 ft]; Length=599 mm; Maximum Air Flow=4790.0 m³/h; Power=704 W; R1=285 mm; R2=290 mm; Ry=199 mm; Sound pressure level at 3 m distance=67 dBA; Temperature of moving air=-25...+60 °C; Weight=15.80 kg; Width=664 mm; Сonnector=No; Сonnector E=No; Сonnector at an angle=Yes
- Centro-M EC 250 L: Amperage=1 A; Apparent Load=170 VA; B=355 mm; B1=395 mm; B2=315 mm; Bracket=Yes; Bracket angle=No; Casing Material=Metal, painted, grey, matt RAL 7040; D=248 mm; D1=345 mm; D2=320 mm; Diameter=248 mm; Dy=244 mm; H=395 mm; H1=223 mm; Height=425 mm; L=250 mm; L1=25 mm  [stored 0.082021 ft]; L2=30 mm  [stored 0.0984252 ft]; L3=40 mm  [stored 0.131234 ft]; L4=55 mm  [stored 0.180446 ft]; Length=250 mm; Maximum Air Flow=985.0 m³/h; Power=100 W; R1=173 mm; R2=178 mm; Ry=124 mm  [stored 0.406824 ft]; Sound pressure level at 3 m distance=44 dBA; Temperature of moving air=-25...+60 °C; Weight=5.09 kg; Width=395 mm; Сonnector=Yes; Сonnector E=No; Сonnector at an angle=No

note: column(s) folded — value = type name in every type: 00_20_Type

note: [stored X ft] marks values corroborated as IEEE doubles in the binary element streams (Revit-internal decimal feet)
